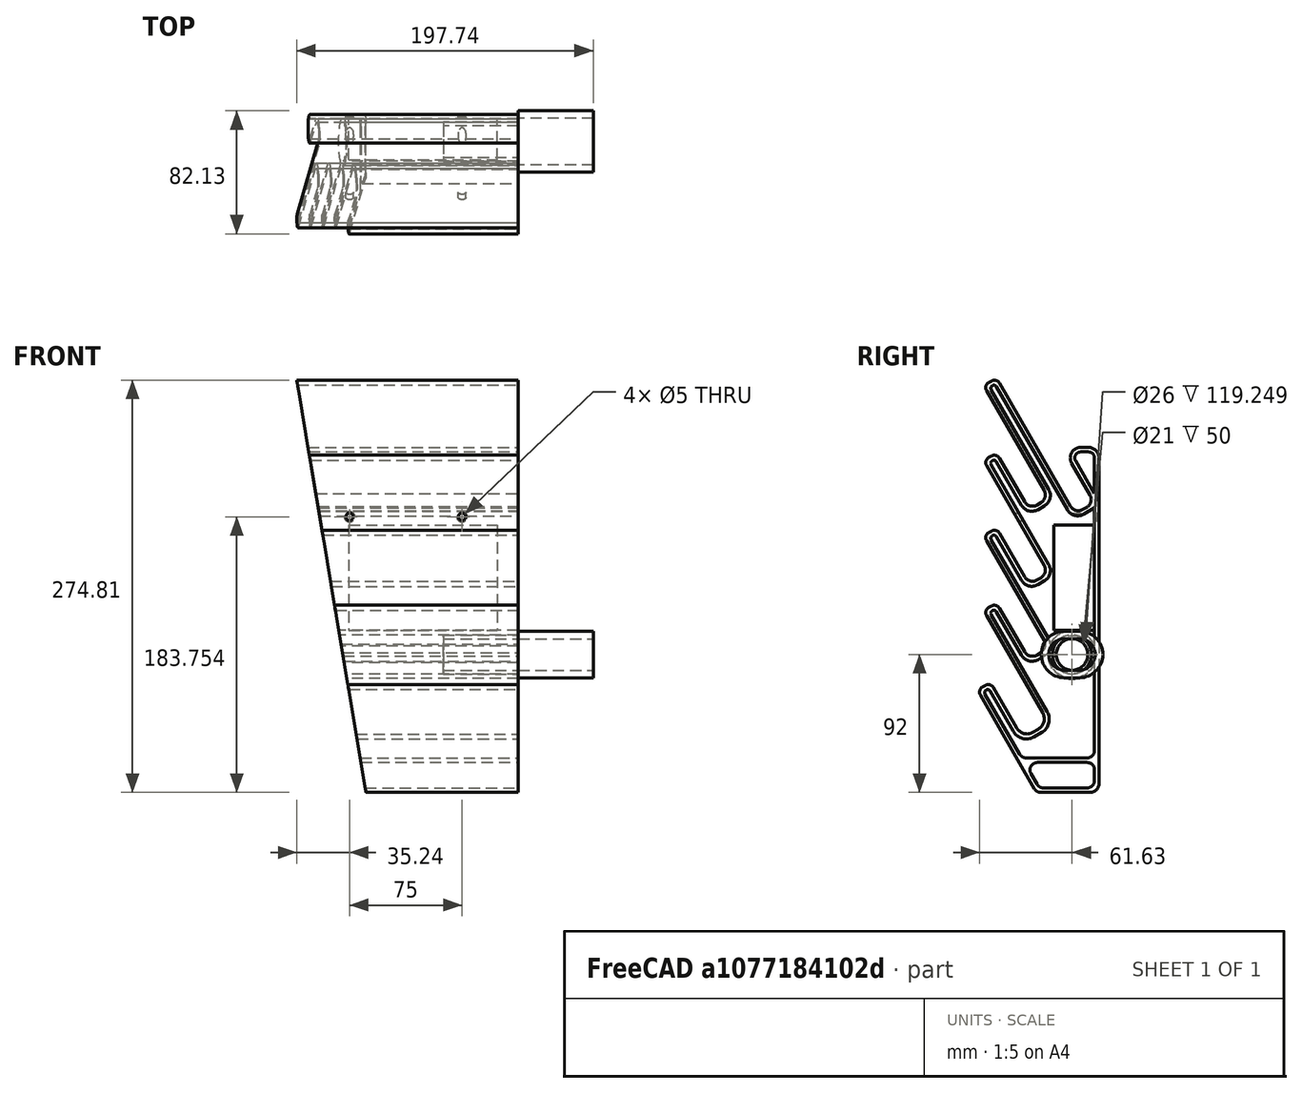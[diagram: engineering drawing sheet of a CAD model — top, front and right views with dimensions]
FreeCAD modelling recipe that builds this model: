
FCSTD DOCUMENT  (FreeCAD 1.0R39109 (Git))
Label: charging_station
License: All rights reserved
LicenseURL: https://en.wikipedia.org/wiki/All_rights_reserved
objects: PartDesign::Fillet×13, Sketcher::SketchObject×8, PartDesign::Pad×5, PartDesign::Body×3, Spreadsheet::Sheet×1, Mesh::Feature×1, PartDesign::Hole×1, PartDesign::Chamfer×1, PartDesign::Pocket×1
note: 82 computed .brp shape members not serialized (recipe doc carries the construction recipe); baked Part::Feature solids carry a one-line shape summary decoded from their .brp

FEATURE [Spreadsheet::Sheet] Spreadsheet  label="dimensions"
  cells = A1='station_depth; B1(station_depth)==150 mm; A2='station_height; B2(station_height)==230 mm; A3='station_width; B3(station_width)==77 mm; A4='station_angle; B4(station_angle)==60 °; A5='wave_thickness; B5(wave_thickness)==3 mm; A6='wave_diameter; B6(wave_diameter)==15 mm; A7='wave_diameter_small; B7(wave_diameter_small)==10 mm; A8='powersupply_length; B8(powersupply_length)==99 mm; A9='powersupply_width; B9(powersupply_width)==70 mm; A10='powersupply_height; B10(powersupply_height)==27 mm
FEATURE [Sketcher::SketchObject] Sketch  label="Sketch (old)"
  ArcFitTolerance = 0
  AttachmentSupport = -> [YZ_Plane]
  FullyConstrained = false
  MakeInternals = false
  MapMode = 5
  Placement = pos=(0,0,0) rot=(0.57735,0.57735,0.57735;2.0944rad)
  expr: Constraints[0] = <<dimensions>>.wave_thickness
  expr: Constraints[144] = 30 mm
  expr: Constraints[159] = <<dimensions>>.wave_thickness
  expr: Constraints[166] = Spreadsheet.wave_diameter
  expr: Constraints[167] = Spreadsheet.wave_diameter + 2 * <<dimensions>>.wave_thickness
  expr: Constraints[180] = <<dimensions>>.wave_thickness
  expr: Constraints[185] = 21 mm - 2 * <<dimensions>>.wave_thickness
  expr: Constraints[187] = 15 mm - 2 * <<dimensions>>.wave_thickness
  expr: Constraints[24] = Spreadsheet.wave_diameter + 2 * <<dimensions>>.wave_thickness + 5 mm
  expr: Constraints[25] = Spreadsheet.wave_diameter + 5 mm
  expr: Constraints[51] = <<dimensions>>.wave_diameter_small
  expr: Constraints[52] = <<dimensions>>.wave_diameter_small - 2 * <<dimensions>>.wave_thickness
  sketch-geometry (67):
    g0: LineSegment StartX=73 StartY=216.694 StartZ=0 EndX=73 EndY=2 EndZ=0
    g1: LineSegment StartX=70 StartY=2 StartZ=0 EndX=70 EndY=216.694 EndZ=0
    g2: Circle CenterX=0 CenterY=58.8565 CenterZ=0 NormalX=0 NormalY=0 NormalZ=1 AngleXU=0 Radius=2
    g3: Circle CenterX=0 CenterY=58.8565 CenterZ=0 NormalX=0 NormalY=0 NormalZ=1 AngleXU=0 Radius=5
    g4: Circle CenterX=0 CenterY=116.856 CenterZ=0 NormalX=0 NormalY=0 NormalZ=1 AngleXU=0 Radius=5
    g5: Circle CenterX=0 CenterY=116.856 CenterZ=0 NormalX=0 NormalY=0 NormalZ=1 AngleXU=0 Radius=2
    g6: Circle CenterX=0 CenterY=166.856 CenterZ=0 NormalX=0 NormalY=0 NormalZ=1 AngleXU=0 Radius=5
    g7: Circle CenterX=0 CenterY=166.856 CenterZ=0 NormalX=0 NormalY=0 NormalZ=1 AngleXU=0 Radius=2
    g8: Circle CenterX=0 CenterY=216.856 CenterZ=0 NormalX=0 NormalY=0 NormalZ=1 AngleXU=0 Radius=5
    g9: Circle CenterX=0 CenterY=216.856 CenterZ=0 NormalX=0 NormalY=0 NormalZ=1 AngleXU=0 Radius=2
    g10: Circle CenterX=0 CenterY=266.856 CenterZ=0 NormalX=0 NormalY=0 NormalZ=1 AngleXU=0 Radius=5
    g11: Circle CenterX=0 CenterY=266.856 CenterZ=0 NormalX=0 NormalY=0 NormalZ=1 AngleXU=0 Radius=2
    g12: Circle CenterX=30 CenterY=43.1817 CenterZ=0 NormalX=0 NormalY=0 NormalZ=1 AngleXU=0 Radius=10
    g13: Circle CenterX=30 CenterY=43.1817 CenterZ=0 NormalX=0 NormalY=0 NormalZ=1 AngleXU=0 Radius=13
    g14: Circle CenterX=30 CenterY=93.0747 CenterZ=0 NormalX=0 NormalY=0 NormalZ=1 AngleXU=0 Radius=7.5
    g15: Circle CenterX=30 CenterY=93.0747 CenterZ=0 NormalX=0 NormalY=0 NormalZ=1 AngleXU=0 Radius=10.5
    g16: Circle CenterX=30 CenterY=143.075 CenterZ=0 NormalX=0 NormalY=0 NormalZ=1 AngleXU=0 Radius=7.5
    g17: Circle CenterX=30 CenterY=143.075 CenterZ=0 NormalX=0 NormalY=0 NormalZ=1 AngleXU=0 Radius=10.5
    g18: Circle CenterX=30 CenterY=193.075 CenterZ=0 NormalX=0 NormalY=0 NormalZ=1 AngleXU=0 Radius=7.5
    g19: Circle CenterX=30 CenterY=193.075 CenterZ=0 NormalX=0 NormalY=0 NormalZ=1 AngleXU=0 Radius=10.5
    g20: LineSegment [constr] StartX=0 StartY=266.856 StartZ=0 EndX=0 EndY=58.8565 EndZ=0
    g21: LineSegment [constr] StartX=-85.4083 StartY=211.856 StartZ=0 EndX=70.2151 EndY=312.073 EndZ=0
    g22: LineSegment [constr] StartX=-85.4083 StartY=161.856 StartZ=0 EndX=70.2151 EndY=262.073 EndZ=0
    g23: LineSegment [constr] StartX=-85.4083 StartY=111.856 StartZ=0 EndX=70.2151 EndY=212.073 EndZ=0
    g24: LineSegment [constr] StartX=-85.4083 StartY=61.8563 StartZ=0 EndX=70.2151 EndY=162.073 EndZ=0
    g25: LineSegment [constr] StartX=-85.4083 StartY=3.85626 StartZ=0 EndX=70.2151 EndY=104.073 EndZ=0
    g26: LineSegment [constr] StartX=-85.4083 StartY=3.85626 StartZ=0 EndX=-85.4083 EndY=211.856 EndZ=0
    g27: LineSegment [constr] StartX=13.2857 StartY=27.6812 StartZ=0 EndX=186.816 EndY=188.61 EndZ=0
    g28: LineSegment [constr] StartX=13.2857 StartY=77.5742 StartZ=0 EndX=186.816 EndY=238.503 EndZ=0
    g29: LineSegment [constr] StartX=13.2857 StartY=127.574 StartZ=0 EndX=186.816 EndY=288.503 EndZ=0
    g30: LineSegment [constr] StartX=30 StartY=43.1817 StartZ=0 EndX=30 EndY=193.075 EndZ=0
    g31: LineSegment StartX=1.68151 StartY=59.9393 StartZ=0 EndX=20.468 EndY=34.3419 EndZ=0
    g32: LineSegment StartX=4.20377 StartY=61.5635 StartZ=0 EndX=22.6677 EndY=36.3819 EndZ=0
    g33: LineSegment StartX=30.2502 StartY=-3.09321 StartZ=0 EndX=-4.20377 EndY=56.1494 EndZ=0
    g34: LineSegment StartX=32.9092 StartY=-1.70415 StartZ=0 EndX=-1.68151 EndY=57.7736 EndZ=0
    g35: LineSegment StartX=37.3323 StartY=49.9815 StartZ=0 EndX=-4.20377 EndY=114.149 EndZ=0
    g36: LineSegment StartX=-1.68151 StartY=115.774 StartZ=0 EndX=39.532 EndY=52.0214 EndZ=0
    g37: LineSegment StartX=1.68151 StartY=117.939 StartZ=0 EndX=22.3011 EndY=85.9349 EndZ=0
    g38: LineSegment StartX=24.5008 StartY=87.9749 StartZ=0 EndX=4.20377 EndY=119.564 EndZ=0
    g39: LineSegment StartX=35.4992 StartY=98.1746 StartZ=0 EndX=-4.20377 EndY=164.149 EndZ=0
    g40: LineSegment StartX=-1.68151 StartY=165.774 StartZ=0 EndX=37.6989 EndY=100.215 EndZ=0
    g41: LineSegment StartX=4.20377 StartY=169.564 StartZ=0 EndX=24.5008 EndY=137.975 EndZ=0
    g42: LineSegment StartX=22.3011 StartY=135.935 StartZ=0 EndX=1.68151 EndY=167.939 EndZ=0
    g43: LineSegment StartX=-1.68151 StartY=215.774 StartZ=0 EndX=37.6989 EndY=150.215 EndZ=0
    g44: LineSegment StartX=4.20377 StartY=219.564 StartZ=0 EndX=24.5008 EndY=187.975 EndZ=0
    g45: LineSegment StartX=-4.20377 StartY=264.149 StartZ=0 EndX=35.4992 EndY=198.175 EndZ=0
    g46: LineSegment StartX=-4.20377 StartY=214.149 StartZ=0 EndX=35.4992 EndY=148.175 EndZ=0
    g47: LineSegment StartX=1.68151 StartY=217.939 StartZ=0 EndX=22.3011 EndY=185.935 EndZ=0
    g48: LineSegment StartX=-1.68151 StartY=265.774 StartZ=0 EndX=37.6989 EndY=200.215 EndZ=0
    g49: LineSegment [constr] StartX=13.2857 StartY=177.574 StartZ=0 EndX=186.816 EndY=338.503 EndZ=0
    g50: LineSegment [constr] StartX=13.2857 StartY=27.6812 StartZ=0 EndX=13.2857 EndY=177.574 EndZ=0
    g51: Circle CenterX=61.2876 CenterY=194.602 CenterZ=0 NormalX=0 NormalY=0 NormalZ=1 AngleXU=0 Radius=7.5
    g52: Circle CenterX=61.2876 CenterY=194.602 CenterZ=0 NormalX=0 NormalY=0 NormalZ=1 AngleXU=0 Radius=10.5
    g53: ArcOfCircle CenterX=40 CenterY=2 CenterZ=0 NormalX=0 NormalY=0 NormalZ=1 AngleXU=0 Radius=11 StartAngle=1.5708 EndAngle=4.71239
    g54: ArcOfCircle CenterX=62 CenterY=2 CenterZ=0 NormalX=0 NormalY=0 NormalZ=1 AngleXU=0 Radius=11 StartAngle=4.71239 EndAngle=7.85398
    g55: LineSegment StartX=40 StartY=-9 StartZ=0 EndX=62 EndY=-9 EndZ=0
    g56: LineSegment StartX=62 StartY=13 StartZ=0 EndX=40 EndY=13 EndZ=0
    g57: ArcOfCircle CenterX=40 CenterY=2 CenterZ=0 NormalX=0 NormalY=0 NormalZ=1 AngleXU=0 Radius=8 StartAngle=1.5708 EndAngle=4.71239
    g58: ArcOfCircle CenterX=62 CenterY=2 CenterZ=0 NormalX=0 NormalY=0 NormalZ=1 AngleXU=0 Radius=8 StartAngle=4.71239 EndAngle=7.85398
    g59: LineSegment StartX=40 StartY=-6 StartZ=0 EndX=62 EndY=-6 EndZ=0
    g60: LineSegment StartX=62 StartY=10 StartZ=0 EndX=40 EndY=10 EndZ=0
    g61: LineSegment StartX=4.20377 StartY=269.564 StartZ=0 EndX=54.4246 EndY=191.577 EndZ=0
    g62: LineSegment StartX=1.68151 StartY=267.939 StartZ=0 EndX=51.725 EndY=190.265 EndZ=0
    g63: Circle CenterX=65.5 CenterY=216.694 CenterZ=0 NormalX=0 NormalY=0 NormalZ=1 AngleXU=0 Radius=4.5
    g64: Circle CenterX=65.5 CenterY=216.694 CenterZ=0 NormalX=0 NormalY=0 NormalZ=1 AngleXU=0 Radius=7.5
    g65: LineSegment StartX=65.9431 StartY=200.482 StartZ=0 EndX=58.9474 EndY=213.045 EndZ=0
    g66: LineSegment StartX=63.1165 StartY=212.877 StartZ=0 EndX=70.2153 EndY=200.129 EndZ=0
  constraints (200):
    c: DistanceX(g1,g0) = 3
    c: Horizontal(g0,g1)
    c: Coincident(g3,g2)
    c: Coincident(g5,g4)
    c: Coincident(g7,g6)
    c: Coincident(g9,g8)
    c: Coincident(g11,g10)
    c: Equal(g2,g5)
    c: Equal(g5,g7)
    c: Equal(g7,g9)
    c: Equal(g9,g11)
    c: Equal(g3,g4)
    c: Equal(g4,g6)
    c: Equal(g6,g8)
    c: Equal(g8,g10)
    c: Coincident(g13,g12)
    c: Coincident(g15,g14)
    c: Coincident(g17,g16)
    c: Coincident(g19,g18)
    c: Equal(g15,g17)
    c: Equal(g17,g19)
    c: Equal(g14,g16)
    c: Equal(g16,g18)
    c: Distance(g13,g1) = 27
    c: Diameter(g13) = 26
    c: Diameter(g12) = 20
    c: Coincident(g20,g10)
    c: Coincident(g20,g2)
    c: Vertical(g20)
    c: PointOnObject(g4,g20)
    c: PointOnObject(g6,g20)
    c: PointOnObject(g8,g20)
    c: PointOnObject(g10,g21)
    c: Equal(g21,g22)
    c: Equal(g22,g23)
    c: Equal(g23,g24)
    c: Equal(g24,g25)
    c: PointOnObject(g8,g22)
    c: PointOnObject(g6,g23)
    c: PointOnObject(g4,g24)
    c: PointOnObject(g2,g25)
    c: Parallel(g25,g24)
    c: Parallel(g24,g23)
    c: Parallel(g23,g22)
    c: Parallel(g22,g21)
    c: Coincident(g26,g25)
    c: Coincident(g26,g21)
    c: Vertical(g26)
    c: PointOnObject(g22,g26)
    c: PointOnObject(g23,g26)
    c: PointOnObject(g24,g26)
    c: Diameter(g3) = 10
    c: Diameter(g2) = 4
    c: PointOnObject(g16,g29)
    c: PointOnObject(g14,g28)
    c: PointOnObject(g12,g27)
    c: Equal(g27,g28)
    c: Equal(g28,g29)
    c: Parallel(g27,g28)
    c: Parallel(g28,g29)
    c: Coincident(g30,g12)
    c: Coincident(g30,g18)
    c: PointOnObject(g16,g30)
    c: PointOnObject(g14,g30)
    c: Parallel(g0,g1)
    c: Vertical(g1)
    c: PointOnObject(g31,g2)
    c: PointOnObject(g31,g13)
    c: PointOnObject(g32,g3)
    c: PointOnObject(g32,g12)
    c: PointOnObject(g33,g3)
    c: PointOnObject(g34,g2)
    c: PointOnObject(g33,g25)
    c: PointOnObject(g34,g25)
    c: PointOnObject(g31,g25)
    c: PointOnObject(g32,g25)
    c: PointOnObject(g32,g27)
    c: PointOnObject(g31,g27)
    c: PointOnObject(g35,g12)
    c: PointOnObject(g35,g4)
    c: PointOnObject(g36,g5)
    c: PointOnObject(g36,g13)
    c: PointOnObject(g37,g5)
    c: PointOnObject(g37,g15)
    c: PointOnObject(g38,g14)
    c: PointOnObject(g38,g4)
    c: PointOnObject(g35,g24)
    c: PointOnObject(g36,g24)
    c: PointOnObject(g37,g24)
    c: PointOnObject(g38,g24)
    c: PointOnObject(g36,g27)
    c: PointOnObject(g35,g27)
    c: PointOnObject(g37,g28)
    c: PointOnObject(g38,g28)
    c: PointOnObject(g39,g14)
    c: PointOnObject(g39,g6)
    c: PointOnObject(g40,g7)
    c: PointOnObject(g41,g6)
    c: PointOnObject(g41,g16)
    c: PointOnObject(g42,g17)
    c: PointOnObject(g42,g7)
    c: PointOnObject(g43,g9)
    c: PointOnObject(g44,g8)
    c: PointOnObject(g44,g18)
    c: PointOnObject(g45,g10)
    c: PointOnObject(g45,g18)
    c: PointOnObject(g39,g28)
    c: PointOnObject(g40,g28)
    c: PointOnObject(g40,g15)
    c: PointOnObject(g39,g23)
    c: PointOnObject(g40,g23)
    c: PointOnObject(g42,g23)
    c: PointOnObject(g41,g23)
    c: PointOnObject(g42,g29)
    c: PointOnObject(g41,g29)
    c: PointOnObject(g43,g29)
    c: PointOnObject(g43,g17)
    c: PointOnObject(g44,g22)
    c: PointOnObject(g46,g8)
    c: PointOnObject(g46,g16)
    c: PointOnObject(g46,g22)
    c: PointOnObject(g46,g29)
    c: PointOnObject(g43,g22)
    c: PointOnObject(g47,g9)
    c: PointOnObject(g47,g19)
    c: PointOnObject(g47,g22)
    c: PointOnObject(g45,g21)
    c: PointOnObject(g48,g11)
    c: PointOnObject(g48,g19)
    c: Equal(g29,g49)
    c: Parallel(g29,g49)
    c: PointOnObject(g18,g49)
    c: PointOnObject(g47,g49)
    c: PointOnObject(g44,g49)
    c: PointOnObject(g45,g49)
    c: PointOnObject(g48,g49)
    c: Coincident(g50,g27)
    c: Coincident(g50,g49)
    c: Vertical(g50)
    c: PointOnObject(g29,g50)
    c: PointOnObject(g28,g50)
    c: Parallel(g50,g30)
    c: PointOnObject(g48,g21)
    c: PointOnObject(g2,g-2)
    c: DistanceX(g-1,g12) = 30
    c: Coincident(g52,g51)
    c: Tangent(g53,g55) = -1.5708
    c: Tangent(g55,g54) = -1.5708
    c: Tangent(g54,g56) = -1.5708
    c: Tangent(g56,g53) = -1.5708
    c: Equal(g53,g54)
    c: Horizontal(g55)
    c: Tangent(g57,g59) = -1.5708
    c: Tangent(g59,g58) = -1.5708
    c: Tangent(g58,g60) = -1.5708
    c: Tangent(g60,g57) = -1.5708
    c: Equal(g57,g58)
    c: Coincident(g57,g53)
    c: Coincident(g54,g58)
    c: DistanceY(g58,g54) = 3
    c: PointOnObject(g61,g10)
    c: PointOnObject(g61,g51)
    c: Tangent(g61,g10)
    c: PointOnObject(g62,g11)
    c: PointOnObject(g62,g52)
    c: Coincident(g64,g63)
    c: Diameter(g14) = 15
    c: Diameter(g15) = 21
    c: DistanceY(g4,g6) = 50
    c: DistanceY(g6,g8) = 50
    c: DistanceY(g8,g10) = 50
    c: DistanceY(g2,g4) = 58
    c: DistanceY(g14,g16) = 50
    c: DistanceY(g16,g18) = 50
    c: PointOnObject(g33,g53)
    c: PointOnObject(g34,g57)
    c: Diameter(g57) = 16
    c: DistanceX(g57,g58) = 22
    c: DistanceY(g-1,g53) = 2
    c: DistanceX(g-1,g53) = 40
    c: Distance(g33,g34) = 3
    c: Parallel(g33,g34)
    c: PointOnObject(g62,g21)
    c: PointOnObject(g61,g21)
    c: Diameter(g52) = 21
    c: Diameter(g51) = 15
    c: Diameter(g64) = 15
    c: Diameter(g63) = 9
    c: PointOnObject(g65,g51)
    c: PointOnObject(g65,g64)
    c: Tangent(g65,g64)
    c: PointOnObject(g66,g63)
    c: PointOnObject(g66,g52)
    c: Parallel(g66,g65)
    c: Angle(g43,g47) = 0.0314159
    c: Angle(g48,g62) = 0.0314159
    c: PointOnObject(g1,g58)
    c: PointOnObject(g0,g64)
    c: PointOnObject(g1,g63)
    c: Horizontal(g63,g1)
FEATURE [Mesh::Feature] chargercut_widened_nosupportr_correctedcurve_chargercut
  Placement = pos=(-90,78.5,9) rot=(1,0,0;1.5708rad)
FEATURE [Sketcher::SketchObject] Sketch001
  ArcFitTolerance = 0
  AttachmentSupport = -> [YZ_Plane]
  FullyConstrained = true
  MakeInternals = false
  MapMode = 5
  Placement = pos=(0,0,0) rot=(0.57735,0.57735,0.57735;2.0944rad)
  expr: Constraints[100] = <<dimensions>>.wave_thickness
  expr: Constraints[101] = <<dimensions>>.wave_thickness
  expr: Constraints[102] = <<dimensions>>.wave_thickness
  expr: Constraints[103] = <<dimensions>>.wave_thickness
  expr: Constraints[104] = <<dimensions>>.wave_thickness
  expr: Constraints[105] = <<dimensions>>.wave_thickness
  expr: Constraints[106] = <<dimensions>>.wave_thickness
  expr: Constraints[107] = <<dimensions>>.wave_thickness
  expr: Constraints[108] = <<dimensions>>.wave_thickness
  expr: Constraints[109] = <<dimensions>>.wave_thickness
  expr: Constraints[110] = <<dimensions>>.wave_thickness
  expr: Constraints[111] = <<dimensions>>.wave_thickness
  expr: Constraints[112] = <<dimensions>>.wave_thickness
  expr: Constraints[113] = <<dimensions>>.wave_thickness
  expr: Constraints[114] = <<dimensions>>.wave_thickness
  expr: Constraints[115] = <<dimensions>>.wave_thickness
  expr: Constraints[116] = <<dimensions>>.wave_thickness
  expr: Constraints[117] = <<dimensions>>.wave_thickness
  expr: Constraints[118] = <<dimensions>>.wave_thickness
  expr: Constraints[119] = <<dimensions>>.wave_thickness
  expr: Constraints[120] = <<dimensions>>.wave_thickness
  expr: Constraints[121] = <<dimensions>>.wave_thickness
  expr: Constraints[122] = <<dimensions>>.wave_thickness
  expr: Constraints[126] = <<dimensions>>.wave_diameter
  expr: Constraints[127] = <<dimensions>>.wave_diameter + 5 mm
  expr: Constraints[142] = <<dimensions>>.station_height
  expr: Constraints[143] = <<dimensions>>.station_width
  expr: Constraints[145] = <<dimensions>>.station_angle
  expr: Constraints[146] = <<dimensions>>.powersupply_height - 0.5 mm
  expr: Constraints[153] = <<dimensions>>.wave_thickness
  expr: Constraints[157] = <<dimensions>>.wave_thickness
  expr: Constraints[87] = <<dimensions>>.wave_thickness
  expr: Constraints[88] = <<dimensions>>.wave_thickness
  expr: Constraints[95] = <<dimensions>>.wave_diameter_small
  sketch-geometry (53):
    g0: LineSegment StartX=77 StartY=-10 StartZ=0 EndX=35.3756 EndY=-10 EndZ=0
    g1: LineSegment StartX=35.3756 StartY=-10 StartZ=0 EndX=-4.09808 EndY=58.3705 EndZ=0
    g2: LineSegment StartX=-4.09808 StartY=58.3705 StartZ=0 EndX=4.56218 EndY=63.3705 EndZ=0
    g3: LineSegment StartX=4.56218 StartY=63.3705 StartZ=0 EndX=26.0814 EndY=26.0981 EndZ=0
    g4: LineSegment StartX=26.0814 StartY=26.0981 StartZ=0 EndX=43.4019 EndY=36.0981 EndZ=0
    g5: LineSegment StartX=43.4019 StartY=36.0981 StartZ=0 EndX=0 EndY=111.272 EndZ=0
    g6: LineSegment StartX=0 StartY=111.272 StartZ=0 EndX=8.66025 EndY=116.272 EndZ=0
    g7: LineSegment StartX=8.66025 StartY=116.272 StartZ=0 EndX=30.4115 EndY=78.5981 EndZ=0
    g8: LineSegment StartX=30.4115 StartY=78.5981 StartZ=0 EndX=43.4019 EndY=86.0981 EndZ=0
    g9: LineSegment StartX=43.4019 StartY=86.0981 StartZ=0 EndX=0 EndY=161.272 EndZ=0
    g10: LineSegment StartX=0 StartY=161.272 StartZ=0 EndX=8.66025 EndY=166.272 EndZ=0
    g11: LineSegment StartX=8.66025 StartY=166.272 StartZ=0 EndX=30.4115 EndY=128.598 EndZ=0
    g12: LineSegment StartX=30.4115 StartY=128.598 StartZ=0 EndX=43.4019 EndY=136.098 EndZ=0
    g13: LineSegment StartX=43.4019 StartY=136.098 StartZ=0 EndX=0 EndY=211.272 EndZ=0
    g14: LineSegment StartX=0 StartY=211.272 StartZ=0 EndX=8.66025 EndY=216.272 EndZ=0
    g15: LineSegment StartX=8.66025 StartY=216.272 StartZ=0 EndX=30.4115 EndY=178.598 EndZ=0
    g16: LineSegment StartX=30.4115 StartY=178.598 StartZ=0 EndX=43.4019 EndY=186.098 EndZ=0
    g17: LineSegment StartX=43.4019 StartY=186.098 StartZ=0 EndX=0 EndY=261.272 EndZ=0
    g18: LineSegment StartX=0 StartY=261.272 StartZ=0 EndX=8.66025 EndY=266.272 EndZ=0
    g19: LineSegment StartX=8.66025 StartY=266.272 StartZ=0 EndX=61.0096 EndY=175.601 EndZ=0
    g20: LineSegment StartX=61.0096 StartY=175.601 StartZ=0 EndX=74 EndY=183.101 EndZ=0
    g21: LineSegment StartX=74 StartY=183.101 StartZ=0 EndX=52.6962 EndY=220 EndZ=0
    g22: LineSegment StartX=52.6962 StartY=220 StartZ=0 EndX=77 EndY=220 EndZ=0
    g23: LineSegment StartX=77 StartY=220 StartZ=0 EndX=77 EndY=-10 EndZ=0
    g24: LineSegment StartX=37.1077 StartY=-7 StartZ=0 EndX=27.2927 EndY=10 EndZ=0
    g25: LineSegment StartX=0 StartY=57.2724 StartZ=0 EndX=3.4641 EndY=59.2724 EndZ=0
    g26: LineSegment StartX=3.4641 StartY=59.2724 StartZ=0 EndX=24.9833 EndY=22 EndZ=0
    g27: LineSegment StartX=24.9833 StartY=22 StartZ=0 EndX=47.5 EndY=35 EndZ=0
    g28: LineSegment StartX=47.5 StartY=35 StartZ=0 EndX=4.09808 EndY=110.174 EndZ=0
    g29: LineSegment StartX=4.09808 StartY=110.174 StartZ=0 EndX=7.56218 EndY=112.174 EndZ=0
    g30: LineSegment StartX=7.56218 StartY=112.174 StartZ=0 EndX=29.3135 EndY=74.5 EndZ=0
    g31: LineSegment StartX=29.3135 StartY=74.5 StartZ=0 EndX=47.5 EndY=85 EndZ=0
    g32: LineSegment StartX=47.5 StartY=85 StartZ=0 EndX=4.09808 EndY=160.174 EndZ=0
    g33: LineSegment StartX=4.09808 StartY=160.174 StartZ=0 EndX=7.56218 EndY=162.174 EndZ=0
    g34: LineSegment StartX=7.56218 StartY=162.174 StartZ=0 EndX=29.3135 EndY=124.5 EndZ=0
    g35: LineSegment StartX=29.3135 StartY=124.5 StartZ=0 EndX=47.5 EndY=135 EndZ=0
    g36: LineSegment StartX=47.5 StartY=135 StartZ=0 EndX=4.09808 EndY=210.174 EndZ=0
    g37: LineSegment StartX=4.09808 StartY=210.174 StartZ=0 EndX=7.56218 EndY=212.174 EndZ=0
    g38: LineSegment StartX=7.56218 StartY=212.174 StartZ=0 EndX=29.3135 EndY=174.5 EndZ=0
    g39: LineSegment StartX=29.3135 StartY=174.5 StartZ=0 EndX=47.5 EndY=185 EndZ=0
    g40: LineSegment StartX=47.5 StartY=185 StartZ=0 EndX=4.09808 EndY=260.174 EndZ=0
    g41: LineSegment StartX=4.09808 StartY=260.174 StartZ=0 EndX=7.56218 EndY=262.174 EndZ=0
    g42: LineSegment StartX=7.56218 StartY=262.174 StartZ=0 EndX=59.9115 EndY=171.503 EndZ=0
    g43: LineSegment StartX=59.9115 StartY=171.503 StartZ=0 EndX=74 EndY=179.637 EndZ=0
    g44: LineSegment StartX=74 StartY=189.101 StartZ=0 EndX=57.8923 EndY=217 EndZ=0
    g45: LineSegment StartX=57.8923 StartY=217 StartZ=0 EndX=74 EndY=217 EndZ=0
    g46: LineSegment StartX=74 StartY=217 StartZ=0 EndX=74 EndY=189.101 EndZ=0
    g47: LineSegment StartX=74 StartY=-7 StartZ=0 EndX=37.1077 EndY=-7 EndZ=0
    g48: LineSegment StartX=74 StartY=179.637 StartZ=0 EndX=74 EndY=13 EndZ=0
    g49: LineSegment StartX=25.5607 StartY=13 StartZ=0 EndX=74 EndY=13 EndZ=0
    g50: LineSegment StartX=27.2927 StartY=10 StartZ=0 EndX=74 EndY=10 EndZ=0
    g51: LineSegment StartX=25.5607 StartY=13 StartZ=0 EndX=0 EndY=57.2724 EndZ=0
    g52: LineSegment StartX=74 StartY=10 StartZ=0 EndX=74 EndY=-7 EndZ=0
  constraints (160):
    c: Horizontal(g0)
    c: Coincident(g1,g2)
    c: Coincident(g2,g3)
    c: Coincident(g3,g4)
    c: Coincident(g4,g5)
    c: Coincident(g5,g6)
    c: Coincident(g6,g7)
    c: Coincident(g7,g8)
    c: Coincident(g8,g9)
    c: Coincident(g9,g10)
    c: Coincident(g10,g11)
    c: Coincident(g11,g12)
    c: Coincident(g12,g13)
    c: Coincident(g13,g14)
    c: Coincident(g14,g15)
    c: Coincident(g15,g16)
    c: Coincident(g16,g17)
    c: PointOnObject(g17,g-2)
    c: Coincident(g17,g18)
    c: Coincident(g18,g19)
    c: Coincident(g19,g20)
    c: Coincident(g20,g21)
    c: Coincident(g21,g22)
    c: Coincident(g22,g23)
    c: Vertical(g23)
    c: PointOnObject(g51,g-2)
    c: Coincident(g51,g25)
    c: Coincident(g25,g26)
    c: Coincident(g26,g27)
    c: Coincident(g27,g28)
    c: Coincident(g28,g29)
    c: Coincident(g29,g30)
    c: Coincident(g30,g31)
    c: Coincident(g31,g32)
    c: Coincident(g32,g33)
    c: Coincident(g33,g34)
    c: Coincident(g34,g35)
    c: Coincident(g35,g36)
    c: Coincident(g36,g37)
    c: Coincident(g37,g38)
    c: Coincident(g38,g39)
    c: Coincident(g39,g40)
    c: Coincident(g40,g41)
    c: Coincident(g41,g42)
    c: Coincident(g42,g43)
    c: Coincident(g44,g45)
    c: Coincident(g45,g46)
    c: Vertical(g46)
    c: Coincident(g52,g47)
    c: Horizontal(g47)
    c: Parallel(g1,g24)
    c: Parallel(g24,g26)
    c: Parallel(g26,g3)
    c: Parallel(g3,g5)
    c: Parallel(g5,g28)
    c: Parallel(g28,g30)
    c: Parallel(g30,g7)
    c: Parallel(g7,g9)
    c: Parallel(g9,g32)
    c: Parallel(g32,g34)
    c: Parallel(g34,g11)
    c: Parallel(g11,g13)
    c: Parallel(g13,g36)
    c: Parallel(g36,g38)
    c: Parallel(g38,g15)
    c: Parallel(g15,g17)
    c: Parallel(g17,g40)
    c: Parallel(g40,g42)
    c: Parallel(g42,g19)
    c: Parallel(g19,g21)
    c: Parallel(g21,g44)
    c: Parallel(g43,g20)
    c: Parallel(g20,g39)
    c: Parallel(g39,g16)
    c: Parallel(g16,g35)
    c: Parallel(g35,g12)
    c: Parallel(g12,g31)
    c: Parallel(g31,g8)
    c: Parallel(g8,g27)
    c: Parallel(g27,g4)
    c: Parallel(g29,g6)
    c: Parallel(g25,g2)
    c: Parallel(g33,g10)
    c: Parallel(g37,g14)
    c: Parallel(g41,g18)
    c: Parallel(g45,g22)
    c: Horizontal(g22)
    c: DistanceX(g52,g0) = 3
    c: DistanceY(g0,g52) = 3
    c: Perpendicular(g25,g24)
    c: Perpendicular(g29,g28)
    c: Perpendicular(g33,g32)
    c: Perpendicular(g37,g36)
    c: Perpendicular(g41,g40)
    c: Perpendicular(g4,g3)
    c: Distance(g1,g2) = 10
    c: Equal(g2,g6)
    c: Equal(g6,g10)
    c: Equal(g10,g14)
    c: Equal(g14,g18)
    c: Distance(g51,g2) = 3
    c: Distance(g51,g1) = 3
    c: Distance(g25,g3) = 3
    c: Distance(g3,g27) = 3
    c: Distance(g7,g31) = 3
    c: Distance(g11,g35) = 3
    c: Distance(g15,g39) = 3
    c: Distance(g19,g43) = 3
    c: Distance(g44,g22) = 3
    c: Distance(g20,g44) = 3
    c: Distance(g28,g5) = 3
    c: Distance(g28,g6) = 3
    c: Distance(g29,g7) = 3
    c: Distance(g32,g9) = 3
    c: Distance(g32,g10) = 3
    c: Distance(g33,g11) = 3
    c: Distance(g36,g13) = 3
    c: Distance(g36,g14) = 3
    c: Distance(g37,g15) = 3
    c: Distance(g40,g17) = 3
    c: Distance(g40,g18) = 3
    c: Distance(g41,g19) = 3
    c: Distance(g45,g23) = 3
    c: Equal(g8,g12)
    c: Equal(g12,g16)
    c: Equal(g16,g20)
    c: Distance(g8) = 15
    c: Distance(g4) = 20
    c: DistanceY(g0,g-1) = 10
    c: Vertical(g27,g31)
    c: Vertical(g31,g35)
    c: Vertical(g35,g39)
    c: Coincident(g47,g24)
    c: Coincident(g0,g1)
    c: Coincident(g46,g44)
    c: Coincident(g48,g43)
    c: PointOnObject(g5,g-2)
    c: PointOnObject(g9,g-2)
    c: PointOnObject(g13,g-2)
    c: Coincident(g23,g0)
    c: Vertical(g43,g44)
    c: DistanceY(g-1,g27) = 35
    c: DistanceY(g23,g23) = 230
    c: DistanceX(g-1,g0) = 77
    c: Vertical(g43,g20)
    c: Angle(g1,g-1) = 1.0472
    c: Distance(g27,g48) = 26.5
    c: Horizontal(g49)
    c: Horizontal(g50)
    c: Coincident(g24,g50)
    c: Coincident(g51,g49)
    c: Coincident(g48,g49)
    c: Coincident(g52,g50)
    c: DistanceY(g50,g48) = 3
    c: Parallel(g1,g51)
    c: Parallel(g1,g24)
    c: Parallel(g52,g23)
    c: Distance(g24,g1) = 3
    c: DistanceY(g-1,g50) = 10
    c: Vertical(g48,g50)
FEATURE [PartDesign::Pad] Pad  label="profile"
  Direction = (1,0,0)
  Length = 150
  Length2 = 10
  Placement = pos=(0,0,0) rot=(1,1,1;2.0944rad)
  Profile = -> Sketch001
  ReferenceAxis = -> Sketch001 [N_Axis]
  Suppressed = false
  Type = 0
  expr: Length = <<dimensions>>.station_depth
FEATURE [PartDesign::Fillet] Fillet
  Base = -> Pad [Edge5,Edge8,Edge17,Edge20,Edge29,Edge32,Edge41,Edge44,Edge53,Edge56]
  BaseFeature = -> Pad
  Placement = pos=(0,0,0) rot=(1,1,1;2.0944rad)
  Radius = 4
  SupportTransform = false
  Suppressed = false
  UseAllEdges = false
FEATURE [PartDesign::Fillet] Fillet001
  Base = -> Fillet [Edge163,Edge162,Edge167,Edge166,Edge170,Edge171,Edge175,Edge174,Edge179,Edge178]
  BaseFeature = -> Fillet
  Placement = pos=(0,0,0) rot=(1,1,1;2.0944rad)
  Radius = 1.9
  SupportTransform = false
  Suppressed = false
  UseAllEdges = false
FEATURE [PartDesign::Fillet] Fillet002
  Base = -> Fillet001 [Edge93,Edge89]
  BaseFeature = -> Fillet001
  Placement = pos=(0,0,0) rot=(1,1,1;2.0944rad)
  Radius = 10
  SupportTransform = false
  Suppressed = false
  UseAllEdges = false
FEATURE [PartDesign::Fillet] Fillet003
  Base = -> Fillet002 [Edge163,Edge159]
  BaseFeature = -> Fillet002
  Placement = pos=(0,0,0) rot=(1,1,1;2.0944rad)
  Radius = 8
  SupportTransform = false
  Suppressed = false
  UseAllEdges = false
FEATURE [PartDesign::Fillet] Fillet004
  Base = -> Fillet003 [Edge185,Edge181,Edge205,Edge209,Edge203,Edge199]
  BaseFeature = -> Fillet003
  Placement = pos=(0,0,0) rot=(1,1,1;2.0944rad)
  Radius = 8
  SupportTransform = false
  Suppressed = false
  UseAllEdges = false
FEATURE [PartDesign::Fillet] Fillet005
  Base = -> Fillet004 [Edge219,Edge195,Edge199,Edge223,Edge225,Edge221]
  BaseFeature = -> Fillet004
  Placement = pos=(0,0,0) rot=(1,1,1;2.0944rad)
  Radius = 6
  SupportTransform = false
  Suppressed = false
  UseAllEdges = false
FEATURE [PartDesign::Fillet] Fillet006
  Base = -> Fillet005 [Edge235]
  BaseFeature = -> Fillet005
  Placement = pos=(0,0,0) rot=(1,1,1;2.0944rad)
  Radius = 8
  SupportTransform = false
  Suppressed = false
  UseAllEdges = false
FEATURE [PartDesign::Fillet] Fillet007
  Base = -> Fillet006 [Edge242,Edge238]
  BaseFeature = -> Fillet006
  Placement = pos=(0,0,0) rot=(1,1,1;2.0944rad)
  Radius = 6
  SupportTransform = false
  Suppressed = false
  UseAllEdges = false
FEATURE [PartDesign::Fillet] Fillet008
  Base = -> Fillet007 [Edge272,Edge274]
  BaseFeature = -> Fillet007
  Placement = pos=(0,0,0) rot=(1,1,1;2.0944rad)
  Radius = 4
  SupportTransform = false
  Suppressed = false
  UseAllEdges = false
FEATURE [PartDesign::Fillet] Fillet009
  Base = -> Fillet008 [Edge106,Edge110]
  BaseFeature = -> Fillet008
  Placement = pos=(0,0,0) rot=(1,1,1;2.0944rad)
  Radius = 7
  SupportTransform = false
  Suppressed = false
  UseAllEdges = false
FEATURE [PartDesign::Fillet] Fillet010
  Base = -> Fillet009 [Edge204,Edge208,Edge284,Edge282,Edge281,Edge286]
  BaseFeature = -> Fillet009
  Placement = pos=(0,0,0) rot=(1,1,1;2.0944rad)
  Radius = 5
  SupportTransform = false
  Suppressed = false
  UseAllEdges = false
FEATURE [PartDesign::Fillet] Fillet011
  Base = -> Fillet010 [Edge204]
  BaseFeature = -> Fillet010
  Placement = pos=(0,0,0) rot=(1,1,1;2.0944rad)
  Radius = 6
  SupportTransform = false
  Suppressed = false
  UseAllEdges = false
FEATURE [PartDesign::Fillet] Fillet012
  Base = -> Fillet011 [Edge111]
  BaseFeature = -> Fillet011
  Placement = pos=(0,0,0) rot=(1,1,1;2.0944rad)
  Radius = 5
  SupportTransform = false
  Suppressed = false
  UseAllEdges = false
FEATURE [Sketcher::SketchObject] Sketch002
  ArcFitTolerance = 0
  AttachmentOffset = pos=(0,0,1) rot=(0,0,1;0rad)
  AttachmentSupport = -> [XZ_Plane]
  FullyConstrained = false
  MakeInternals = false
  MapMode = 5
  Placement = pos=(0,-1,2e-16) rot=(1,0,0;1.5708rad)
  sketch-geometry (3):
    g0: LineSegment StartX=0 StartY=-19.2186 StartZ=0 EndX=0 EndY=278.271 EndZ=0
    g1: LineSegment StartX=0 StartY=278.271 StartZ=0 EndX=50 EndY=-19.2186 EndZ=0
    g2: LineSegment StartX=50 StartY=-19.2186 StartZ=0 EndX=0 EndY=-19.2186 EndZ=0
  constraints (8):
    c: PointOnObject(g0,g-2)
    c: Vertical(g0)
    c: Coincident(g0,g1)
    c: Coincident(g1,g2)
    c: Coincident(g2,g0)
    c: Horizontal(g2)
    c: DistanceY(g0,g0) = 297.49
    c: DistanceX(g2,g2) = 50
FEATURE [Sketcher::SketchObject] Sketch003
  ArcFitTolerance = 0
  AttachmentSupport = -> [YZ_Plane]
  FullyConstrained = true
  MakeInternals = false
  MapMode = 5
  Placement = pos=(0,0,0) rot=(0.57735,0.57735,0.57735;2.0944rad)
  sketch-geometry (2):
    g0: Circle CenterX=59 CenterY=82 CenterZ=0 NormalX=0 NormalY=0 NormalZ=1 AngleXU=0 Radius=13
    g1: Circle CenterX=59 CenterY=82 CenterZ=0 NormalX=0 NormalY=0 NormalZ=1 AngleXU=0 Radius=16
  constraints (5):
    c: Coincident(g1,g0)
    c: Diameter(g1) = 32
    c: Diameter(g0) = 26
    c: DistanceX(g0) = 59
    c: DistanceY(g-1,g0) = 82
FEATURE [PartDesign::Pad] Pad001
  BaseFeature = -> Fillet012
  Direction = (1,0,0)
  Length = 150
  Length2 = 10
  Placement = pos=(0,0,0) rot=(1,1,1;2.0944rad)
  Profile = -> Sketch003
  ReferenceAxis = -> Sketch003 [N_Axis]
  Suppressed = false
  Type = 0
  expr: Length = <<dimensions>>.station_depth
FEATURE [Sketcher::SketchObject] Sketch004
  ArcFitTolerance = 0
  AttachmentSupport = -> [XZ_Plane]
  FullyConstrained = false
  MakeInternals = false
  MapMode = 5
  Placement = pos=(0,0,0) rot=(1,0,0;1.5708rad)
  expr: Constraints[3] = <<dimensions>>.station_depth / 2
  expr: Constraints[4] = <<dimensions>>.station_depth / 4
  sketch-geometry (2):
    g0: Circle CenterX=37.5 CenterY=173.754 CenterZ=0 NormalX=0 NormalY=0 NormalZ=1 AngleXU=0 Radius=2.5
    g1: Circle CenterX=112.5 CenterY=173.754 CenterZ=0 NormalX=0 NormalY=0 NormalZ=1 AngleXU=0 Radius=2.5
  constraints (5):
    c: Horizontal(g0,g1)
    c: Equal(g0,g1)
    c: Diameter(g0) = 5
    c: DistanceX(g0,g1) = 75
    c: DistanceX(g-1,g0) = 37.5
FEATURE [PartDesign::Hole] Hole
  BaseFeature = -> Pad001
  CustomThreadClearance = 0
  Depth = 654.535
  DepthType = 1
  Diameter = 5
  DrillForDepth = false
  DrillPoint = 1
  DrillPointAngle = 118
  HoleCutCountersinkAngle = 90
  HoleCutCustomValues = false
  HoleCutDepth = 0
  HoleCutDiameter = 6.1
  HoleCutType = 0
  ModelThread = false
  Placement = pos=(0,0,0) rot=(1,1,1;2.0944rad)
  Profile = -> Sketch004
  Suppressed = false
  Tapered = false
  TaperedAngle = 90
  ThreadClass = 0
  ThreadDepth = 654.535
  ThreadDepthType = 0
  ThreadDirection = 0
  ThreadFit = 0
  ThreadSize = 0
  ThreadType = 0
  Threaded = false
  UseCustomThreadClearance = false
FEATURE [PartDesign::Chamfer] Chamfer
  Angle = 45
  Base = -> Hole [Edge338,Edge339]
  BaseFeature = -> Hole
  ChamferType = 0
  FlipDirection = false
  Placement = pos=(0,0,0) rot=(1,1,1;2.0944rad)
  Size = 1
  Size2 = 1
  SupportTransform = false
  Suppressed = false
  UseAllEdges = false
FEATURE [PartDesign::Pocket] Pocket
  BaseFeature = -> Chamfer
  Direction = (0,1,-2e-16)
  Length = 5
  Length2 = 5
  Midplane = true
  Placement = pos=(0,0,0) rot=(1,1,1;2.0944rad)
  Profile = -> Sketch002
  ReferenceAxis = -> Sketch002 [N_Axis]
  Suppressed = false
  Type = 1
FEATURE [PartDesign::Body] Body  label="Körper"
  AllowCompound = false
  Group = -> [Sketch,Sketch001,Pad,Fillet,Fillet001,Fillet002,Fillet003,Fillet004,Fillet005,Fillet006,Fillet007,Fillet008,Fillet009,Fillet010,Fillet011,Fillet012,Sketch003,Pad001,Sketch004,Hole,Chamfer,Sketch002,Pocket]
  Origin = -> Origin
  Tip = -> Pocket
FEATURE [Sketcher::SketchObject] Sketch005
  ArcFitTolerance = 0
  AttachmentSupport = -> [YZ_Plane001]
  FullyConstrained = false
  MakeInternals = false
  MapMode = 5
  Placement = pos=(0,0,0) rot=(0.57735,0.57735,0.57735;2.0944rad)
  expr: Constraints[10] = <<dimensions>>.station_width - <<dimensions>>.wave_thickness - <<dimensions>>.powersupply_height
  expr: Constraints[8] = <<dimensions>>.powersupply_height
  expr: Constraints[9] = <<dimensions>>.powersupply_width
  sketch-geometry (4):
    g0: LineSegment StartX=47 StartY=168.233 StartZ=0 EndX=74 EndY=168.233 EndZ=0
    g1: LineSegment StartX=74 StartY=168.233 StartZ=0 EndX=74 EndY=98.233 EndZ=0
    g2: LineSegment StartX=74 StartY=98.233 StartZ=0 EndX=47 EndY=98.233 EndZ=0
    g3: LineSegment StartX=47 StartY=98.233 StartZ=0 EndX=47 EndY=168.233 EndZ=0
  constraints (11):
    c: Coincident(g0,g1)
    c: Coincident(g1,g2)
    c: Coincident(g2,g3)
    c: Coincident(g3,g0)
    c: Horizontal(g0)
    c: Horizontal(g2)
    c: Vertical(g1)
    c: Vertical(g3)
    c: DistanceX(g0,g0) = 27
    c: DistanceY(g1,g1) = 70
    c: DistanceX(g2) = 47
FEATURE [PartDesign::Pad] Pad002
  Direction = (1,0,0)
  Length = 99
  Length2 = 10
  Placement = pos=(0,0,0) rot=(1,1,1;2.0944rad)
  Profile = -> Sketch005
  ReferenceAxis = -> Sketch005 [N_Axis]
  Suppressed = false
  Type = 0
FEATURE [PartDesign::Body] Body001  label="Anker PowerPort 6"
  AllowCompound = false
  Group = -> [Sketch005,Pad002]
  Origin = -> Origin001
  Placement = pos=(37,0,0) rot=(0,0,1;0rad)
  Tip = -> Pad002
FEATURE [Sketcher::SketchObject] Sketch007
  ArcFitTolerance = 1e-06
  AttachmentOffset = pos=(0,0,150) rot=(0,0,1;0rad)
  AttachmentSupport = -> [YZ_Plane002]
  FullyConstrained = true
  MakeInternals = false
  MapMode = 5
  Placement = pos=(150,0,0) rot=(0.57735,0.57735,0.57735;2.0944rad)
  expr: .AttachmentOffset.Base.z = <<dimensions>>.station_depth
  sketch-geometry (2):
    g0: Circle CenterX=59 CenterY=82 CenterZ=0 NormalX=0 NormalY=0 NormalZ=1 AngleXU=0 Radius=10.5
    g1: Circle CenterX=59 CenterY=82 CenterZ=0 NormalX=0 NormalY=0 NormalZ=1 AngleXU=0 Radius=13
  constraints (5):
    c: Coincident(g1,g0)
    c: DistanceX(g-1,g0) = 59
    c: DistanceY(g-1,g0) = 82
    c: Diameter(g1) = 26
    c: Diameter(g0) = 21
FEATURE [PartDesign::Pad] Pad003
  Direction = (1,0,0)
  Length = 50
  Length2 = 10
  Placement = pos=(0,0,0) rot=(1,1,1;2.0944rad)
  Profile = -> Sketch007
  ReferenceAxis = -> Sketch007 [N_Axis]
  Refine = true
  Reversed = true
  Suppressed = false
  Type = 0
FEATURE [Sketcher::SketchObject] Sketch008
  ArcFitTolerance = 1e-06
  AttachmentOffset = pos=(0,0,150) rot=(0,0,1;0rad)
  AttachmentSupport = -> [YZ_Plane002]
  FullyConstrained = true
  MakeInternals = false
  MapMode = 5
  Placement = pos=(150,0,0) rot=(0.57735,0.57735,0.57735;2.0944rad)
  expr: .AttachmentOffset.Base.z = <<dimensions>>.station_depth
  expr: Constraints[17] = 59 mm - 5 mm
  sketch-geometry (8):
    g0: ArcOfCircle CenterX=54 CenterY=82 CenterZ=0 NormalX=0 NormalY=0 NormalZ=1 AngleXU=0 Radius=15.5 StartAngle=1.5708 EndAngle=4.71239
    g1: ArcOfCircle CenterX=64 CenterY=82 CenterZ=0 NormalX=0 NormalY=0 NormalZ=1 AngleXU=0 Radius=15.5 StartAngle=4.71239 EndAngle=7.85398
    g2: LineSegment StartX=54 StartY=97.5 StartZ=0 EndX=64 EndY=97.5 EndZ=0
    g3: LineSegment StartX=54 StartY=66.5 StartZ=0 EndX=64 EndY=66.5 EndZ=0
    g4: ArcOfCircle CenterX=54 CenterY=82 CenterZ=0 NormalX=0 NormalY=0 NormalZ=1 AngleXU=0 Radius=10.5 StartAngle=1.5708 EndAngle=4.71239
    g5: ArcOfCircle CenterX=64 CenterY=82 CenterZ=0 NormalX=0 NormalY=0 NormalZ=1 AngleXU=0 Radius=10.5 StartAngle=4.71239 EndAngle=7.85398
    g6: LineSegment StartX=54 StartY=92.5 StartZ=0 EndX=64 EndY=92.5 EndZ=0
    g7: LineSegment StartX=54 StartY=71.5 StartZ=0 EndX=64 EndY=71.5 EndZ=0
  constraints (18):
    c: Tangent(g0,g2) = 1.5708
    c: Tangent(g0,g3) = -1.5708
    c: Tangent(g1,g2) = 1.5708
    c: Tangent(g1,g3) = -1.5708
    c: Equal(g0,g1)
    c: Horizontal(g2)
    c: Diameter(g0) = 31
    c: Tangent(g4,g6) = 1.5708
    c: Tangent(g4,g7) = -1.5708
    c: Tangent(g5,g6) = 1.5708
    c: Tangent(g5,g7) = -1.5708
    c: Equal(g4,g5)
    c: Coincident(g4,g0)
    c: Coincident(g5,g1)
    c: Diameter(g4) = 21
    c: DistanceX(g0,g1) = 10
    c: DistanceY(g-1,g0) = 82
    c: DistanceX(g-1,g0) = 54
FEATURE [PartDesign::Pad] Pad004
  BaseFeature = -> Pad003
  Direction = (1,0,0)
  Length = 50
  Length2 = 10
  Placement = pos=(0,0,0) rot=(1,1,1;2.0944rad)
  Profile = -> Sketch008
  ReferenceAxis = -> Sketch008 [N_Axis]
  Refine = true
  Suppressed = false
  Type = 0
FEATURE [PartDesign::Body] Body002  label="watch"
  AllowCompound = false
  Group = -> [Sketch007,Pad003,Sketch008,Pad004]
  Origin = -> Origin002
  Tip = -> Pad004
